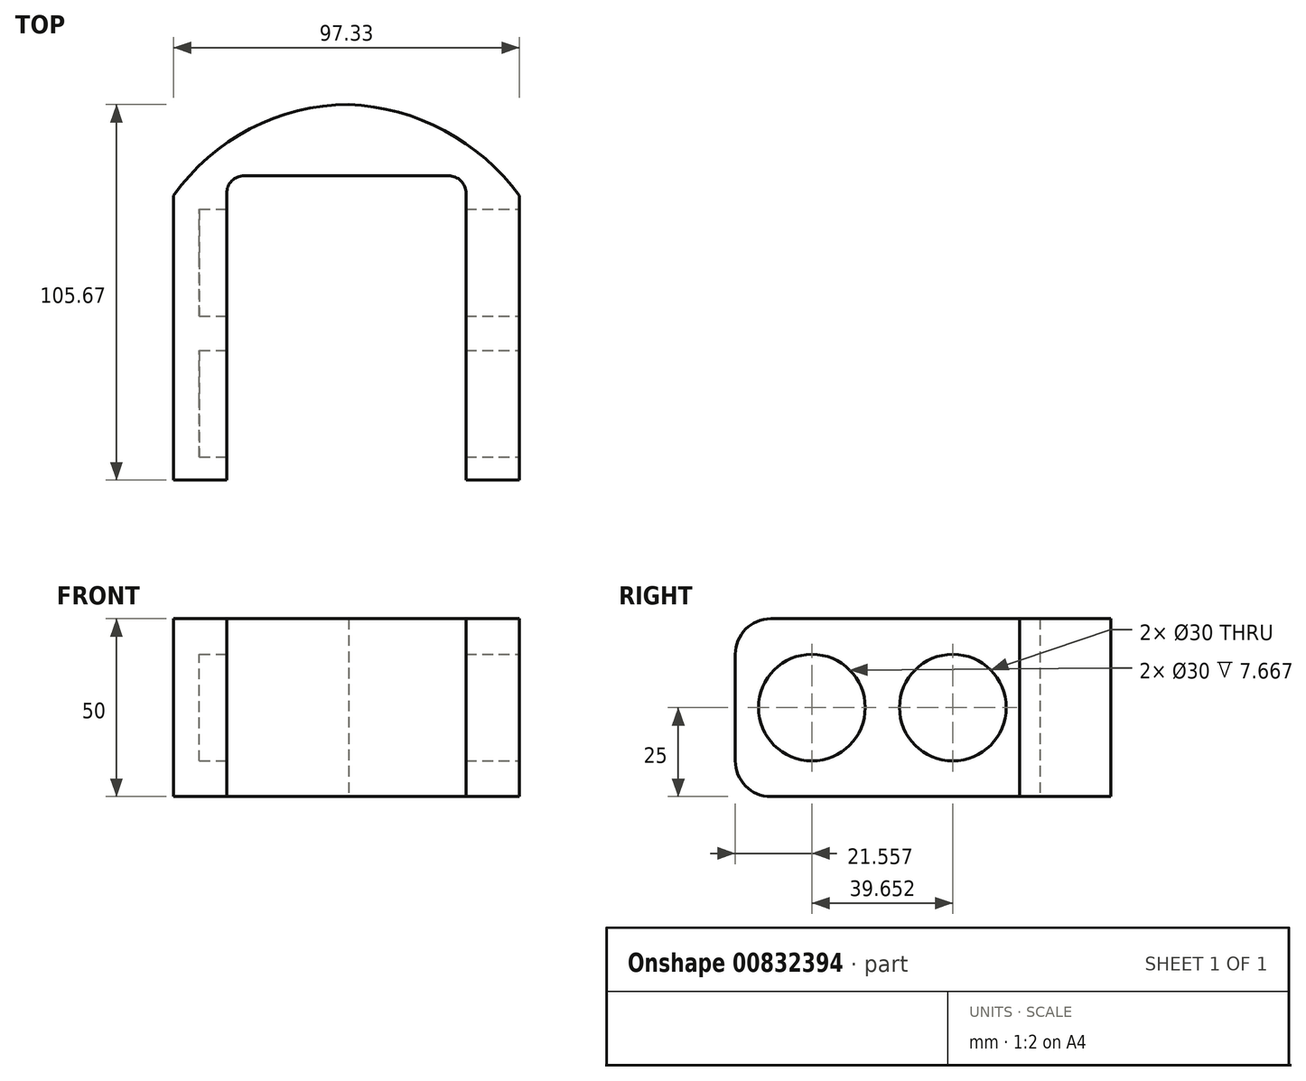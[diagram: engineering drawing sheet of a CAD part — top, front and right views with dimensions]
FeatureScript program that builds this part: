
annotation { "Feature Type Name" : "Feature", "Feature Type Description" : "" }
export const myFeature = defineFeature(function(context is Context, id is Id, definition is map)
    precondition{}
    {
        {
            var Q0;
            Q0=qCreatedBy(makeId("Top.planeOp"),FACE);
            var sketch = newSketch(context, id + "F0", { "sketchPlane" : qUnion([Q0])});
            skLineSegment(sketch, "E0", {"start": v(-53.9, -39.4) * mm, "end": v(-53.9, 40.6) * mm});
            skArc(sketch, "E1", {"start": v(-4.56, 66.27) * mm, "mid": v(-32.33, 59.41) * mm, "end": v(-53.9, 40.6) * mm});
            skArc(sketch, "E2", {"start": v(43.44, 40.6) * mm, "mid": v(22.4, 58.95) * mm, "end": v(-4.56, 66.27) * mm});
            skLineSegment(sketch, "E3", {"start": v(43.44, 40.6) * mm, "end": v(43.44, -39.4) * mm});
            skLineSegment(sketch, "E4", {"start": v(43.44, -39.4) * mm, "end": v(28.44, -39.4) * mm});
            skLineSegment(sketch, "E5", {"start": v(28.44, -39.4) * mm, "end": v(28.44, 46.27) * mm});
            skLineSegment(sketch, "E6", {"start": v(28.44, 46.27) * mm, "end": v(-38.9, 46.27) * mm});
            skLineSegment(sketch, "E7", {"start": v(-38.9, 46.27) * mm, "end": v(-38.9, -39.4) * mm});
            skLineSegment(sketch, "E8", {"start": v(-38.9, -39.4) * mm, "end": v(-53.9, -39.4) * mm});
            skLineSegment(sketch, "E9", {"start": v(-4.56, 66.27) * mm, "end": v(-4.56, 46.27) * mm, "construction": true});
            skSolve(sketch);
        }
        {
            var Q0;
            Q0=makeQuery(id+"F0.imprint","IMPRINT",FACE,{"disambiguationData":[TD([[makeQuery(id+"F0.imprint","IMPRINT",EDGE,{"derivedFrom":sQuery(id+"F0.wireOp",EDGE,"E0")}),-1.0]])]});
            extrude(context, id + "F1", {"entities" : qUnion([Q0]), "depth" : 50 * mm, "offsetDistance" : 25 * mm});
        }
        {
            var Q0;
            Q0=makeQuery(id+"F1.opExtrude","SWEPT_FACE",FACE,{"disambiguationData":[OSD([sQuery(id+"F0.wireOp",EDGE,"E3")])]});
            var sketch = newSketch(context, id + "F2", { "sketchPlane" : qUnion([Q0])});
            skLineSegment(sketch, "E10", {"start": v(-39.4, 25) * mm, "end": v(40.6, 25) * mm, "construction": true});
            skCircle(sketch, "E11", {"center": v(-17.84, 25) * mm, "radius": 15 * mm});
            skCircle(sketch, "E12", {"center": v(21.8, 25) * mm, "radius": 15 * mm});
            skSolve(sketch);
        }
        {
            var Q0;
            Q0=makeQuery(id+"F2.imprint","IMPRINT",FACE,{"disambiguationData":[TD([[makeQuery(id+"F2.imprint","IMPRINT",EDGE,{"derivedFrom":sQuery(id+"F2.wireOp",EDGE,"E11")}),1.0]])]});
            var Q1;
            Q1=makeQuery(id+"F2.imprint","IMPRINT",FACE,{"disambiguationData":[TD([[makeQuery(id+"F2.imprint","IMPRINT",EDGE,{"derivedFrom":sQuery(id+"F2.wireOp",EDGE,"E12")}),1.0]])]});
            extrude(context, id + "F3", {"entities" : qUnion([Q0, Q1]), "operationType" : NewBodyOperationType.REMOVE, "oppositeDirection" : true, "depth" : 90 * mm, "offsetDistance" : 25 * mm});
        }
        {
            var Q0;
            Q0=makeQuery(id+"F1.opExtrude","CAP_EDGE",EDGE,{"disambiguationData":[OSD([sQuery(id+"F0.wireOp",EDGE,"E8")])],"isStart":false});
            var Q1;
            Q1=makeQuery(id+"F1.opExtrude","CAP_EDGE",EDGE,{"disambiguationData":[OSD([sQuery(id+"F0.wireOp",EDGE,"E8")])],"isStart":true});
            var Q2;
            Q2=makeQuery(id+"F1.opExtrude","CAP_EDGE",EDGE,{"disambiguationData":[OSD([sQuery(id+"F0.wireOp",EDGE,"E4")])],"isStart":false});
            var Q3;
            Q3=makeQuery(id+"F1.opExtrude","CAP_EDGE",EDGE,{"disambiguationData":[OSD([sQuery(id+"F0.wireOp",EDGE,"E4")])],"isStart":true});
            fillet(context, id + "F4", {"entities" : qUnion([Q0, Q1, Q2, Q3]), "radius" : 10 * mm, "tangentPropagation" : true, "allowEdgeOverflow" : false});
        }
        {
            var Q0;
            Q0=makeQuery(id+"F1.opExtrude","SWEPT_EDGE",EDGE,{"disambiguationData":[OSD([sQuery(id+"F0.wireOp",EDGE,"E5"),sQuery(id+"F0.wireOp",EDGE,"E6")])]});
            var Q1;
            Q1=makeQuery(id+"F1.opExtrude","SWEPT_EDGE",EDGE,{"disambiguationData":[OSD([sQuery(id+"F0.wireOp",EDGE,"E6"),sQuery(id+"F0.wireOp",EDGE,"E7")])]});
            fillet(context, id + "F5", {"entities" : qUnion([Q0, Q1]), "radius" : 5 * mm, "tangentPropagation" : true, "allowEdgeOverflow" : false});
        }
    });
